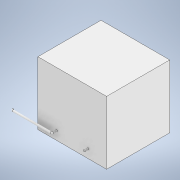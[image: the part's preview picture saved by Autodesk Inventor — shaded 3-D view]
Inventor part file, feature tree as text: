
AUTODESK INVENTOR PART (.ipt)
format: ipt  version: 2022 (Build 260153000, 153)  size: 117,760 bytes
history: native  units: in
note: dims shown in document units (in); Inventor stores cm internally (conversion verified against a paired STEP export)
features: sketch x5, extrude x3, revolve x2, plane x1
ambient origin geometry x8: Origin, YZ Plane, XZ Plane, XY Plane, X Axis, Y Axis, Z Axis, Center Point
bodies: Solid1 (feature_tree)
feature tree (11):
  extrude  "Extrusion1"  Depth=17.0in
  extrude  "Extrusion2"  Depth=17.0in
  plane  "Work Plane1"
  extrude  "Extrusion3"  [1 undecoded]
  revolve  "Revolution1"  Angle=90.0deg
  revolve  "Revolution2"  [1 undecoded]
  sketch  "Sketch1"  dims[d0=18.5in d1=17.0in]
  sketch  "Sketch2"  dims[d2=17.0in d3=0.0in d4=0.5in]
  sketch  "Sketch3"  dims[d5=1.0in d6=0.0in d7=-4.75in]
  sketch  "Sketch4"  dims[d8=10.19in d9=0.0in d10=90.0deg]
  sketch  "Sketch5"  dims[d11=90.0deg]
note: 2 required parameter values undecoded (feature->parameter linkage not recoverable at this tier; creation-order binding heuristic only, values carry confidence <= 0.55)
